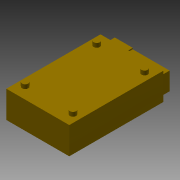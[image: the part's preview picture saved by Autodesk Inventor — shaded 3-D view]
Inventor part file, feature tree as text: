
AUTODESK INVENTOR PART (.ipt)
format: ipt  version: 2016 (Build 200138000, 138)  size: 116,736 bytes
history: native  units: mm
features: extrude x4, sketch x4
ambient origin geometry x8: Origin, YZ Plane, XZ Plane, XY Plane, X Axis, Y Axis, Z Axis, Center Point
bodies: Solid1 (feature_tree)
feature tree (8):
  extrude  "Extrusion1"  Depth=61.5mm
  extrude  "Extrusion2"  Depth=26.4mm
  extrude  "Extrusion3"  Depth=6.0mm
  extrude  "Extrusion4"  Depth=5.25mm
  sketch  "Sketch1"  dims[d0=92.0mm d1=61.5mm]
  sketch  "Sketch3"  dims[d2=26.4mm d3=0.0mm d5=46.75mm]
  sketch  "Sketch4"  dims[d6=69.9mm d7=6.0mm]
  sketch  "Sketch5"  dims[d8=4.0mm d9=0.0mm d10=5.25mm d11=4.0mm d12=15.5mm d13=17.5mm d14=10.0mm d15=0.0mm d16=4.0mm d17=40.0mm d18=2.0mm d19=19.5mm d20=10.0mm d21=0.0mm]
